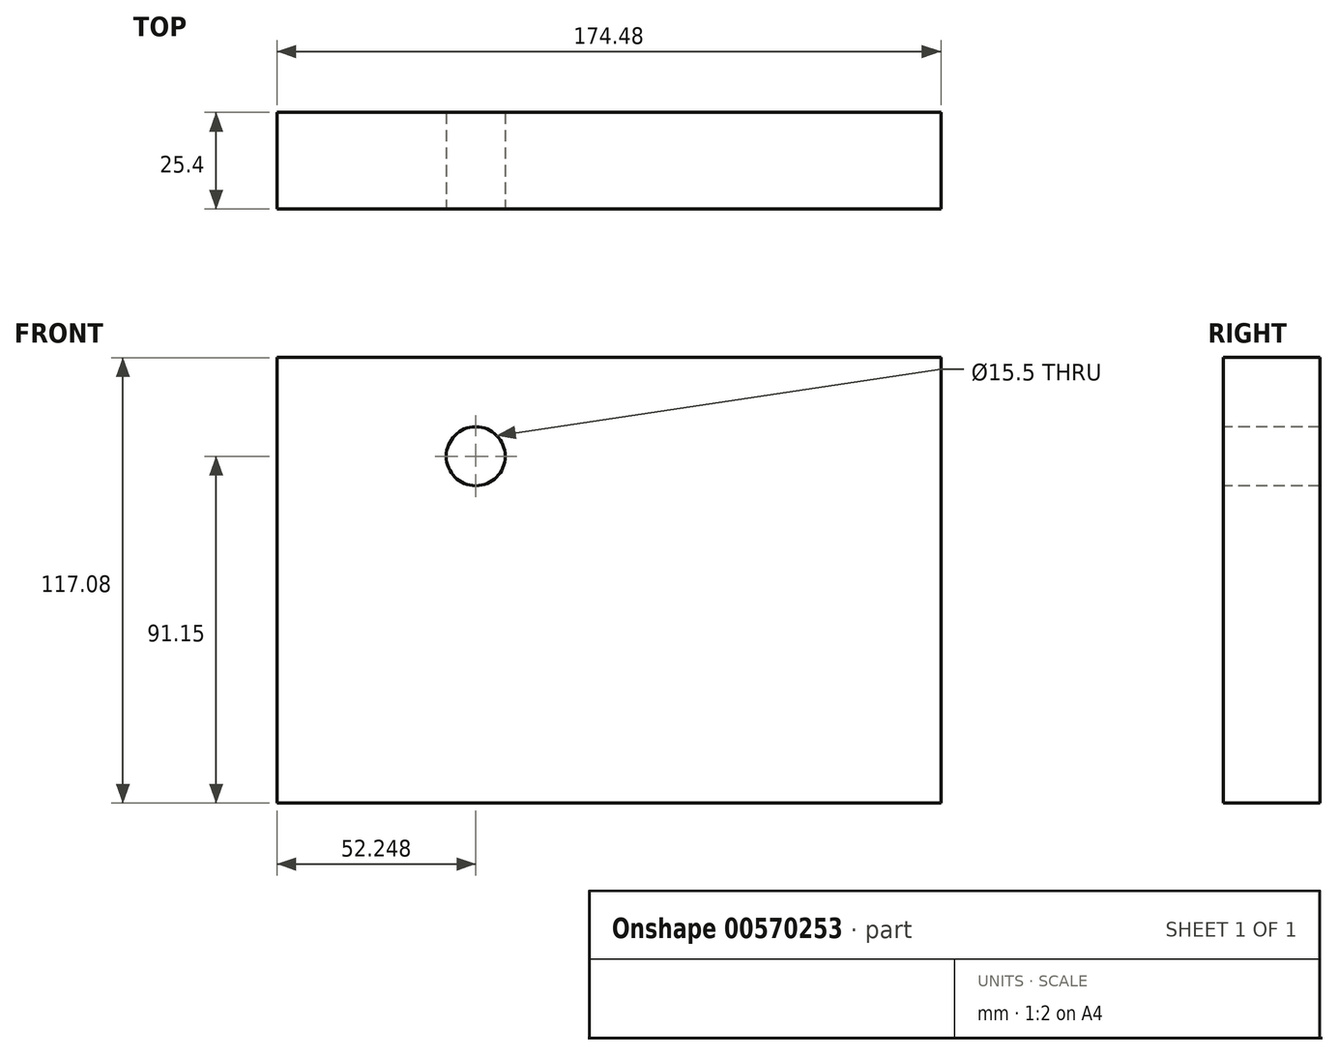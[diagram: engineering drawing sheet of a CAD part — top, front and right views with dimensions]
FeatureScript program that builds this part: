
annotation { "Feature Type Name" : "Feature", "Feature Type Description" : "" }
export const myFeature = defineFeature(function(context is Context, id is Id, definition is map)
    precondition{}
    {
        {
            var Q0;
            Q0=qCreatedBy(makeId("Front.planeOp"),FACE);
            var sketch = newSketch(context, id + "F0", { "sketchPlane" : qUnion([Q0])});
            skLineSegment(sketch, "E0.bottom", {"start": v(-89.45, 51.01) * mm, "end": v(85.03, 51.01) * mm});
            skLineSegment(sketch, "E0.top", {"start": v(-89.45, -66.07) * mm, "end": v(85.03, -66.07) * mm});
            skLineSegment(sketch, "E0.left", {"start": v(-89.45, 51.01) * mm, "end": v(-89.45, -66.07) * mm});
            skLineSegment(sketch, "E0.right", {"start": v(85.03, 51.01) * mm, "end": v(85.03, -66.07) * mm});
            skSolve(sketch);
        }
        {
            var Q0;
            Q0=makeQuery(id+"F0.imprint","IMPRINT",FACE,{"disambiguationData":[TD([[makeQuery(id+"F0.imprint","IMPRINT",EDGE,{"derivedFrom":sQuery(id+"F0.wireOp",EDGE,"E0.bottom")}),-1.0]])]});
            extrude(context, id + "F1", {"entities" : qUnion([Q0]), "depth" : 25.4 * mm, "offsetDistance" : 25.4 * mm});
        }
        {
            var Q0;
            Q0=makeQuery(id+"F1.opExtrude","CAP_FACE",FACE,{"disambiguationData":[OSD([sQuery(id+"F0.wireOp",EDGE,"E0.bottom"),sQuery(id+"F0.wireOp",EDGE,"E0.top"),sQuery(id+"F0.wireOp",EDGE,"E0.left"),sQuery(id+"F0.wireOp",EDGE,"E0.right")])],"isStart":false});
            var sketch = newSketch(context, id + "F2", { "sketchPlane" : qUnion([Q0])});
            skPoint(sketch, "E1", {"position": v(-37.2, 25.08) * mm});
            skSolve(sketch);
        }
        {
            var Q0;
            Q0=sQuery(id+"F2.wireOp",VERTEX,"E1");
            var Q1;
            Q1=makeQuery(id+"F1.opExtrude","SWEPT_BODY",BODY,{"disambiguationData":[OSD([sQuery(id+"F0.wireOp",EDGE,"E0.bottom"),sQuery(id+"F0.wireOp",EDGE,"E0.top"),sQuery(id+"F0.wireOp",EDGE,"E0.left"),sQuery(id+"F0.wireOp",EDGE,"E0.right")])]});
            hole(context, id + "F3", {"style" : HoleStyle.SIMPLE, "endStyle" : HoleEndStyle.THROUGH, "standardTappedOrClearance" : lookupTablePath({ "standard" : "ISO", "fit" : "Normal", "size" : "M14", "type" : "Clearance" }), "standardBlindInLast" : lookupTablePath({ "fit" : "Standard", "standard" : "ISO", "size" : "M14", "type" : "Clearance" }), "holeDiameter" : 15.5 * mm, "isTappedThrough" : true, "tappedDepth" : 12.7 * mm, "tapClearance" : 3, "locations" : qUnion([Q0]), "scope" : qUnion([Q1])});
        }
    });
